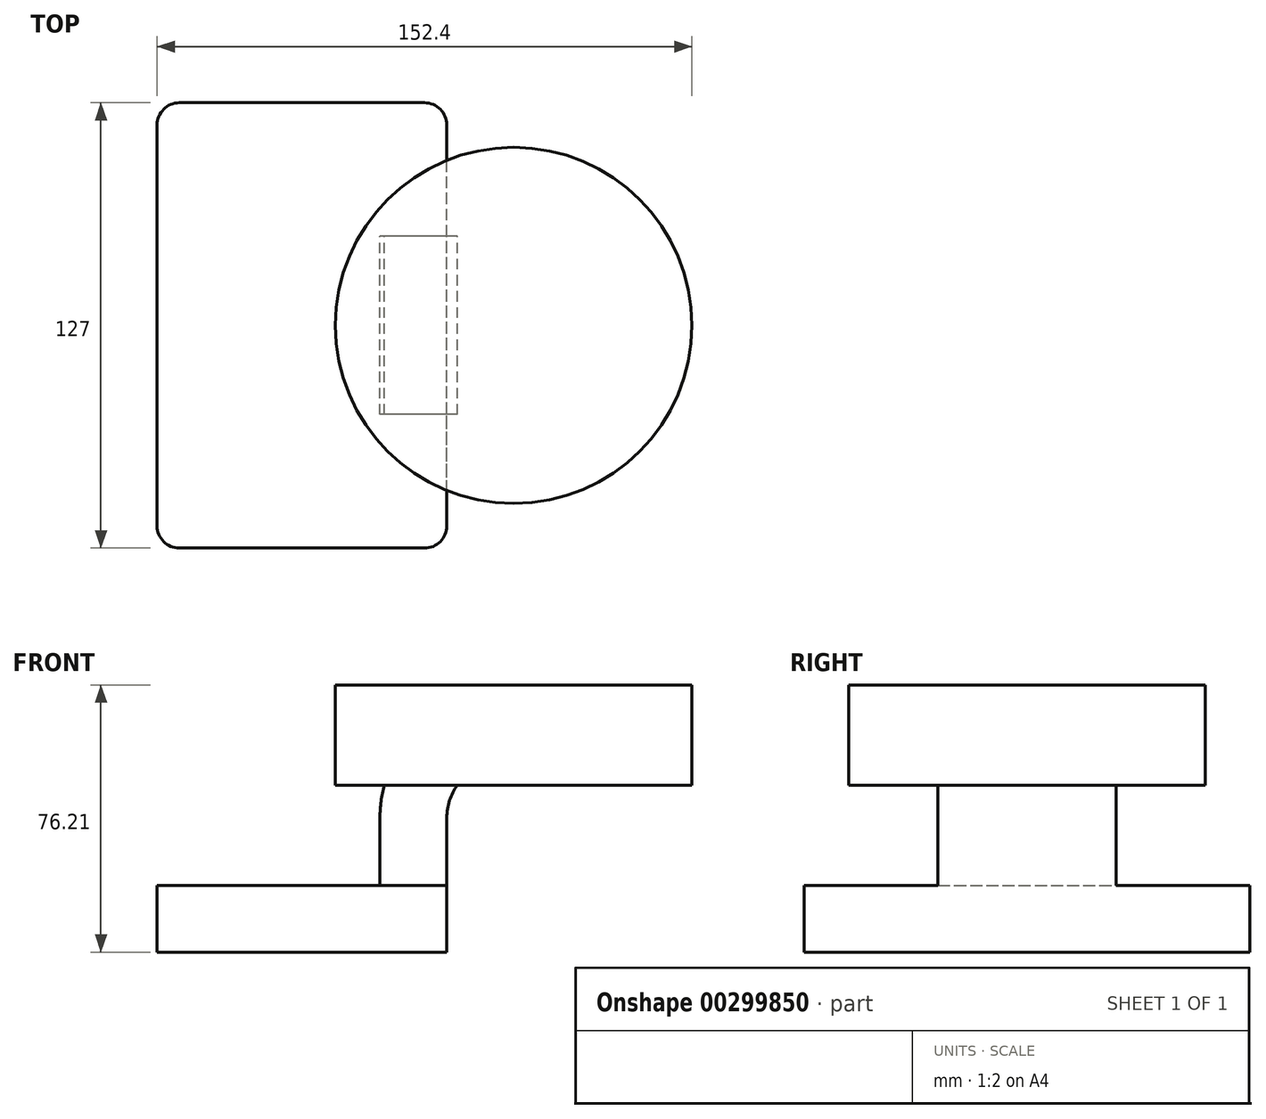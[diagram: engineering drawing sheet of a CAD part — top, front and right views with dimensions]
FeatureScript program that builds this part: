
annotation { "Feature Type Name" : "Feature", "Feature Type Description" : "" }
export const myFeature = defineFeature(function(context is Context, id is Id, definition is map)
    precondition{}
    {
        {
            var Q0;
            Q0=qCreatedBy(makeId("Front.planeOp"),FACE);
            var sketch = newSketch(context, id + "F0", { "sketchPlane" : qUnion([Q0])});
            skLineSegment(sketch, "E0.bottom", {"start": v(41.28, -9.52) * mm, "end": v(-41.28, -9.52) * mm});
            skLineSegment(sketch, "E0.top", {"start": v(41.28, 9.53) * mm, "end": v(-41.28, 9.53) * mm});
            skLineSegment(sketch, "E0.left", {"start": v(41.28, -9.52) * mm, "end": v(41.28, 9.53) * mm});
            skLineSegment(sketch, "E0.right", {"start": v(-41.28, -9.52) * mm, "end": v(-41.28, 9.53) * mm});
            skPoint(sketch, "E0.middle", {"position": v(0, 0) * mm});
            skLineSegment(sketch, "E1.bottom", {"start": v(111.12, 38.1) * mm, "end": v(60.32, 38.1) * mm});
            skLineSegment(sketch, "E1.top", {"start": v(111.12, 66.68) * mm, "end": v(60.32, 66.68) * mm});
            skLineSegment(sketch, "E1.left", {"start": v(111.12, 38.1) * mm, "end": v(111.12, 66.68) * mm});
            skPoint(sketch, "E1.middle", {"position": v(85.72, 52.39) * mm});
            skLineSegment(sketch, "E2", {"start": v(49.79, 42.88) * mm, "end": v(71.19, 42.88) * mm});
            skPoint(sketch, "E3.startSnap0", {"position": v(85.72, 38.1) * mm});
            skLineSegment(sketch, "E4", {"start": v(60.32, 38.1) * mm, "end": v(60.32, 66.68) * mm});
            skLineSegment(sketch, "E5", {"start": v(41.28, 9.53) * mm, "end": v(41.28, 28.81) * mm});
            skArc(sketch, "E6", {"start": v(41.27, 28.81) * mm, "mid": v(43.57, 37.03) * mm, "end": v(49.79, 42.88) * mm});
            skLineSegment(sketch, "E7.0", {"start": v(46.05, 61.93) * mm, "end": v(71.19, 61.93) * mm});
            skArc(sketch, "E7.1", {"start": v(22.23, 28.81) * mm, "mid": v(28.8, 49.2) * mm, "end": v(46.05, 61.93) * mm});
            skLineSegment(sketch, "E7.2", {"start": v(22.23, 9.53) * mm, "end": v(22.23, 28.81) * mm});
            skLineSegment(sketch, "E8", {"start": v(71.19, 42.88) * mm, "end": v(71.19, 61.93) * mm});
            skFitSpline(sketch, "E9", {"points": [v(-41.28, 9.53) * mm, v(46.05, 61.93) * mm], "startDerivative": vector(3.14, 84.12) * mm, "endDerivative": vector(90.15, -9.92) * mm});
            skSolve(sketch);
        }
        {
            var Q0;
            Q0=makeQuery(id+"F0.imprint","IMPRINT",FACE,{"disambiguationData":[TD([[makeQuery(id+"F0.imprint","IMPRINT",EDGE,{"derivedFrom":sQuery(id+"F0.wireOp",EDGE,"E0.bottom")}),-1.0]])]});
            extrude(context, id + "F1", {"entities" : qUnion([Q0]), "endBound" : BoundingType.SYMMETRIC, "depth" : 127 * mm});
        }
        {
            var Q0;
            {var subQ0=sQuery(id+"F0.wireOp",EDGE,"E5");Q0=makeQuery(id+"F0.imprint","IMPRINT",FACE,{"disambiguationData":[TD([[makeQuery(id+"F0.imprint","IMPRINT",EDGE,{"derivedFrom":subQ0}),1.0]])]});}
            var Q1;
            {var subQ0=sQuery(id+"F0.wireOp",EDGE,"E8");Q1=makeQuery(id+"F0.imprint","IMPRINT",FACE,{"disambiguationData":[TD([[makeQuery(id+"F0.imprint","IMPRINT",EDGE,{"derivedFrom":subQ0}),1.0]])]});}
            extrude(context, id + "F2", {"entities" : qUnion([Q0, Q1]), "operationType" : NewBodyOperationType.ADD, "endBound" : BoundingType.SYMMETRIC, "depth" : 50.8 * mm});
        }
        {
            var Q0;
            Q0=makeQuery(id+"F0.imprint","IMPRINT",FACE,{"disambiguationData":[TD([[makeQuery(id+"F0.imprint","IMPRINT",EDGE,{"derivedFrom":sQuery(id+"F0.wireOp",EDGE,"E7.1")}),1.0]])]});
            extrude(context, id + "F3", {"entities" : qUnion([Q0]), "operationType" : NewBodyOperationType.ADD, "endBound" : BoundingType.SYMMETRIC, "depth" : 15.88 * mm});
        }
        {
            var Q0;
            {var subQ5=sQuery(id+"F0.wireOp",EDGE,"E1.bottom");Q0=makeQuery(id+"F0.imprint","IMPRINT",FACE,{"disambiguationData":[TD([[makeQuery(id+"F0.imprint","IMPRINT",EDGE,{"derivedFrom":subQ5}),-1.0]])]});}
            var Q1;
            Q1=sQuery(id+"F0.wireOp",EDGE,"E4");
            revolve(context, id + "F4", {"operationType" : NewBodyOperationType.ADD, "entities" : qUnion([Q0]), "axis" : qUnion([Q1]), "revolveType" : RevolveType.FULL});
        }
        {
            var Q0;
            Q0=makeQuery(id+"F1.opExtrude","CAP_EDGE",EDGE,{"disambiguationData":[OSD([sQuery(id+"F0.wireOp",EDGE,"E0.right")])],"isStart":false});
            var Q1;
            Q1=makeQuery(id+"F1.opExtrude","CAP_EDGE",EDGE,{"disambiguationData":[OSD([sQuery(id+"F0.wireOp",EDGE,"E0.left")])],"isStart":false});
            var Q2;
            Q2=makeQuery(id+"F1.opExtrude","CAP_EDGE",EDGE,{"disambiguationData":[OSD([sQuery(id+"F0.wireOp",EDGE,"E0.left")])],"isStart":true});
            var Q3;
            Q3=makeQuery(id+"F1.opExtrude","CAP_EDGE",EDGE,{"disambiguationData":[OSD([sQuery(id+"F0.wireOp",EDGE,"E0.right")])],"isStart":true});
            fillet(context, id + "F5", {"entities" : qUnion([Q0, Q1, Q2, Q3]), "radius" : 6.35 * mm, "tangentPropagation" : true, "allowEdgeOverflow" : false});
        }
    });
